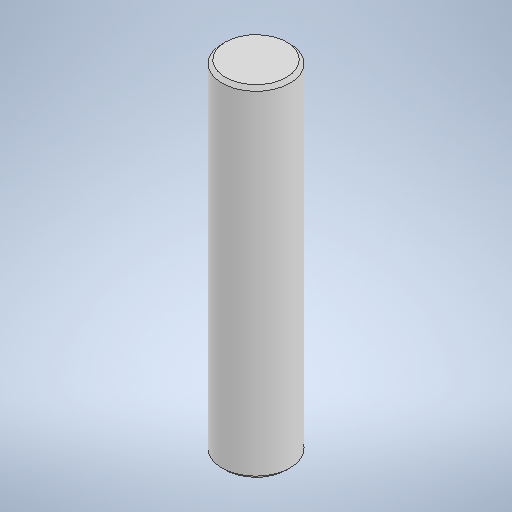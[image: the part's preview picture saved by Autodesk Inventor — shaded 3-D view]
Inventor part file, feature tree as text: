
AUTODESK INVENTOR PART (.ipt)
format: ipt  version: 2025.1 (Build 291241000, 241)  size: 240,640 bytes
history: native  units: mm
features: extrude x1, chamfer x1, sketch x1
ambient origin geometry x8: Origin, YZ Plane, XZ Plane, XY Plane, X Axis, Y Axis, Z Axis, Center Point
bodies: Solid1 (feature_tree)
feature tree (3):
  extrude  "Extrusion1"  Depth=50.0mm TaperAngle=0.0deg
  chamfer  "Chamfer1"  Distance=0.5mm Angle=45.0deg
  sketch  "Sketch1"  dims[d0=10.0mm d1=50.0mm d2=0.0mm d3=0.5mm d4=2.0mm d5=45.0deg]
